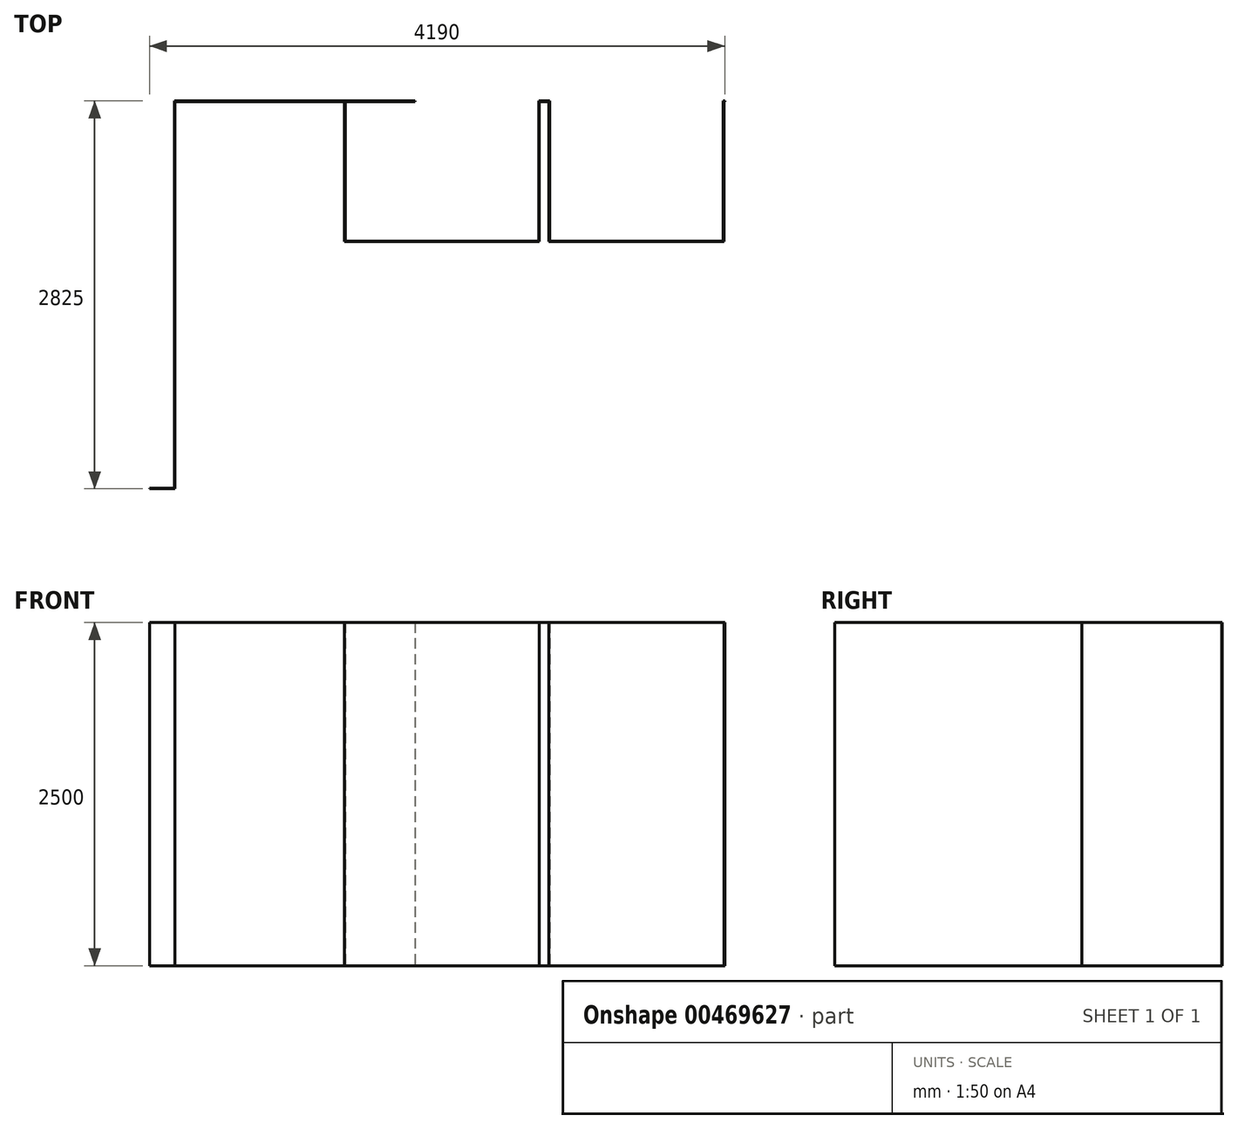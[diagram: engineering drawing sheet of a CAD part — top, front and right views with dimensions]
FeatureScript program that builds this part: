
annotation { "Feature Type Name" : "Feature", "Feature Type Description" : "" }
export const myFeature = defineFeature(function(context is Context, id is Id, definition is map)
    precondition{}
    {
        {
            var Q0;
            Q0=qCreatedBy(makeId("Top.planeOp"),FACE);
            var sketch = newSketch(context, id + "F0", { "sketchPlane" : qUnion([Q0])});
            skLineSegment(sketch, "E0", {"start": v(-542.25, 942.27) * mm, "end": v(867.75, 942.27) * mm});
            skLineSegment(sketch, "E1", {"start": v(867.75, 942.27) * mm, "end": v(867.75, 1962.27) * mm});
            skLineSegment(sketch, "E2", {"start": v(867.75, 1962.27) * mm, "end": v(947.75, 1962.27) * mm});
            skLineSegment(sketch, "E3", {"start": v(947.75, 1962.27) * mm, "end": v(947.75, 942.27) * mm});
            skLineSegment(sketch, "E4", {"start": v(947.75, 942.27) * mm, "end": v(2212.75, 942.27) * mm});
            skLineSegment(sketch, "E5", {"start": v(2212.75, 942.27) * mm, "end": v(2212.75, 1962.27) * mm});
            skLineSegment(sketch, "E6", {"start": v(2212.75, 1962.27) * mm, "end": v(2222.75, 1962.27) * mm});
            skLineSegment(sketch, "E7", {"start": v(-542.25, 942.27) * mm, "end": v(-542.25, 1962.27) * mm});
            skLineSegment(sketch, "E8", {"start": v(-542.25, 1962.27) * mm, "end": v(-32.25, 1962.27) * mm});
            skLineSegment(sketch, "E9", {"start": v(-542.25, 1962.27) * mm, "end": v(-1787.25, 1962.27) * mm});
            skLineSegment(sketch, "E10", {"start": v(-1787.25, 1962.27) * mm, "end": v(-1787.25, -857.73) * mm});
            skLineSegment(sketch, "E11", {"start": v(-1787.25, -857.73) * mm, "end": v(-1967.25, -857.73) * mm});
            skLineSegment(sketch, "E12.0", {"start": v(2217.75, 1957.27) * mm, "end": v(2222.75, 1957.27) * mm});
            skLineSegment(sketch, "E12.1", {"start": v(-547.25, 937.27) * mm, "end": v(-547.25, 1957.27) * mm});
            skLineSegment(sketch, "E12.2", {"start": v(-547.25, 1957.27) * mm, "end": v(-1782.25, 1957.27) * mm});
            skLineSegment(sketch, "E12.3", {"start": v(-1782.25, 1957.27) * mm, "end": v(-1782.25, -862.73) * mm});
            skLineSegment(sketch, "E12.4", {"start": v(-1782.25, -862.73) * mm, "end": v(-1967.25, -862.73) * mm});
            skLineSegment(sketch, "E12.5", {"start": v(-547.25, 937.27) * mm, "end": v(872.75, 937.27) * mm});
            skLineSegment(sketch, "E12.6", {"start": v(872.75, 937.27) * mm, "end": v(872.75, 1957.27) * mm});
            skLineSegment(sketch, "E12.7", {"start": v(872.75, 1957.27) * mm, "end": v(942.75, 1957.27) * mm});
            skLineSegment(sketch, "E12.8", {"start": v(942.75, 1957.27) * mm, "end": v(942.75, 937.27) * mm});
            skLineSegment(sketch, "E12.9", {"start": v(942.75, 937.27) * mm, "end": v(2217.75, 937.27) * mm});
            skLineSegment(sketch, "E12.10", {"start": v(2217.75, 937.27) * mm, "end": v(2217.75, 1957.27) * mm});
            skLineSegment(sketch, "E13", {"start": v(-1967.25, -857.73) * mm, "end": v(-1967.25, -862.73) * mm});
            skLineSegment(sketch, "E14", {"start": v(2222.75, 1962.27) * mm, "end": v(2222.75, 1957.27) * mm});
            skLineSegment(sketch, "E15.0", {"start": v(-542.25, 1957.27) * mm, "end": v(-32.25, 1957.27) * mm});
            skLineSegment(sketch, "E16", {"start": v(-32.25, 1957.27) * mm, "end": v(-32.25, 1962.27) * mm});
            skSolve(sketch);
        }
        {
            var Q0;
            Q0=makeQuery(id+"F0.imprint","IMPRINT",FACE,{"disambiguationData":[TD([[makeQuery(id+"F0.imprint","IMPRINT",EDGE,{"derivedFrom":sQuery(id+"F0.wireOp",EDGE,"VBQ2jNu9-d3M2-l4Gu-QUts-LtF6oqkvU8o2")}),-1.0]])]});
            var Q1;
            {var subQ0=sQuery(id+"F0.wireOp",EDGE,"E0");Q1=makeQuery(id+"F0.imprint","IMPRINT",FACE,{"disambiguationData":[TD([[makeQuery(id+"F0.imprint","IMPRINT",EDGE,{"derivedFrom":subQ0}),-1.0]])]});}
            var Q2;
            {var subQ0=sQuery(id+"F0.wireOp",EDGE,"E8");Q2=makeQuery(id+"F0.imprint","IMPRINT",FACE,{"disambiguationData":[TD([[makeQuery(id+"F0.imprint","IMPRINT",EDGE,{"derivedFrom":subQ0}),-1.0]])]});}
            extrude(context, id + "F1", {"entities" : qUnion([Q0, Q1, Q2]), "depth" : 2500 * mm, "offsetDistance" : 25 * mm});
        }
    });
